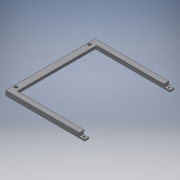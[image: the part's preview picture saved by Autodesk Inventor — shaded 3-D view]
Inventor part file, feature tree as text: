
AUTODESK INVENTOR PART (.ipt)
format: ipt  version: 2016 SP2 (Build 200236200, 236)  size: 169,472 bytes
history: native  units: mm
features: extrude x5, sketch x5, projected_geometry x4
ambient origin geometry x8: Origin, YZ Plane, XZ Plane, XY Plane, X Axis, Y Axis, Z Axis, Center Point
bodies: Volumenkörper1 (feature_tree)
feature tree (14):
  extrude  "Extrusion1"  Depth=9.5mm
  extrude  "Extrusion2"  Depth=150.5mm
  extrude  "Extrusion3"  Depth=1.2mm TaperAngle=0.0deg
  extrude  "Extrusion4"  Depth=8.0mm
  extrude  "Extrusion5"  Depth=8.0mm
  sketch  "Skizze1"  dims[d0=9.5mm d1=9.5mm]
  sketch  "Skizze2"  dims[d2=12.0mm d3=150.5mm]
  sketch  "Skizze3"  dims[d4=127.4mm d5=1.2mm d6=0.0mm]
  projected_geometry  "Projizierte Kontur1"
  projected_geometry  "Projizierte Kontur2"
  sketch  "Skizze4"  dims[d7=10.0mm d8=8.0mm]
  sketch  "Skizze5"  dims[d9=8.0mm d10=8.0mm d11=3.0mm d12=5.0mm d13=4.0mm d14=3.0mm d15=5.0mm d16=4.0mm d17=7.7mm d18=0.0mm d19=5.1mm d20=0.0mm d21=4.0mm d22=5.7mm d23=5.7mm d24=15.0mm d25=15.0mm d26=3.1mm d27=0.0mm d28=3.0mm d29=3.0mm d30=42.55mm d31=0.0mm]
  projected_geometry  "Projizierte Kontur3"
  projected_geometry  "Projizierte Kontur4"
